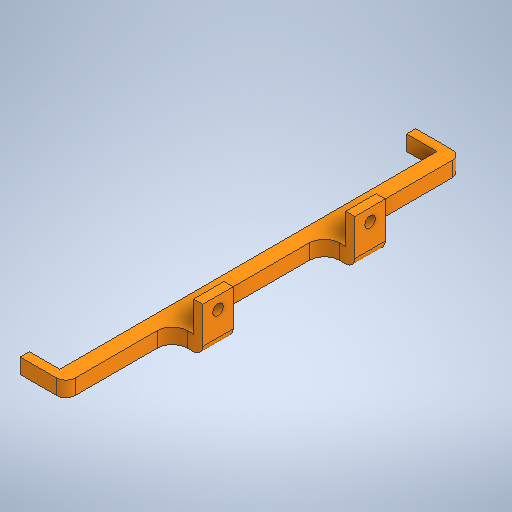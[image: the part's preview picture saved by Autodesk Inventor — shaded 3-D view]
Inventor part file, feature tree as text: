
AUTODESK INVENTOR PART (.ipt)
format: ipt  version: 2025 (Build 290162000, 162)  size: 340,992 bytes
history: native  units: mm
features: extrude x5, sketch x5, fillet x3
ambient origin geometry x8: Origin, YZ Plane, XZ Plane, XY Plane, X Axis, Y Axis, Z Axis, Center Point
bodies: Solide1 (feature_tree)
feature tree (13):
  extrude  "Extrusion1"  Depth=130.0mm
  extrude  "Extrusion2"  Depth=5.0mm
  extrude  "Extrusion3"  Depth=5.0mm TaperAngle=0.0deg
  extrude  "Extrusion4"  Depth=10.0mm
  fillet  "Congé1"  Radius=20.0mm
  fillet  "Congé2"  Radius=10.0mm
  fillet  "Congé3"  Radius=10.0mm
  extrude  "Extrusion5"  Depth=3.5mm
  sketch  "Esquisse1"
  sketch  "Esquisse2"
  sketch  "Esquisse3"
  sketch  "Esquisse4"
  sketch  "Esquisse5"
